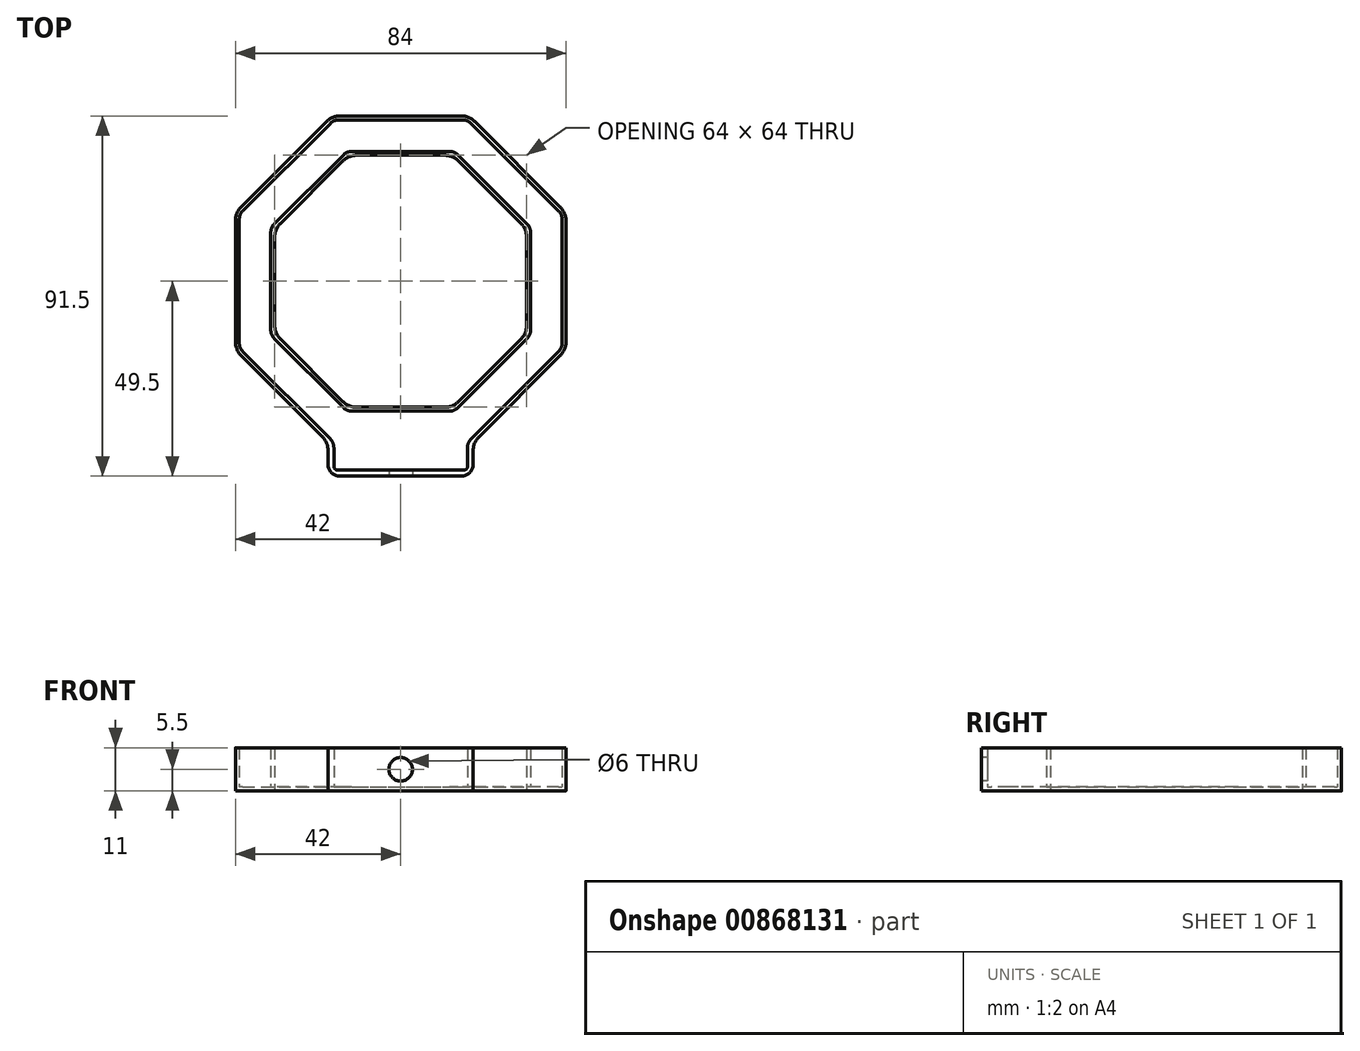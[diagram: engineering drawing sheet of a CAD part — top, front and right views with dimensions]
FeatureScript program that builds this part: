
annotation { "Feature Type Name" : "Feature", "Feature Type Description" : "" }
export const myFeature = defineFeature(function(context is Context, id is Id, definition is map)
    precondition{}
    {
        {
            var Q0;
            Q0=qCreatedBy(makeId("Top.planeOp"),FACE);
            var sketch = newSketch(context, id + "F0", { "sketchPlane" : qUnion([Q0])});
            skCircle(sketch, "E0.cCircle", {"center": v(0, 0) * mm, "radius": 41 * mm, "construction": true});
            skLineSegment(sketch, "E0.0", {"start": v(41, 16.98) * mm, "end": v(41, -16.98) * mm});
            skLineSegment(sketch, "E0.1", {"start": v(41, -16.98) * mm, "end": v(16.98, -41) * mm});
            skLineSegment(sketch, "E0.3", {"start": v(-16.98, -41) * mm, "end": v(-41, -16.98) * mm});
            skLineSegment(sketch, "E0.4", {"start": v(-41, -16.98) * mm, "end": v(-41, 16.98) * mm});
            skLineSegment(sketch, "E0.5", {"start": v(-41, 16.98) * mm, "end": v(-16.98, 41) * mm});
            skLineSegment(sketch, "E0.6", {"start": v(-16.98, 41) * mm, "end": v(16.98, 41) * mm});
            skLineSegment(sketch, "E0.7", {"start": v(16.98, 41) * mm, "end": v(41, 16.98) * mm});
            skPoint(sketch, "E0.0.midPoint", {"position": v(41, 0) * mm});
            skCircle(sketch, "E1.cCircle", {"center": v(0, 0) * mm, "radius": 33 * mm, "construction": true});
            skLineSegment(sketch, "E1.0", {"start": v(-33, 13.67) * mm, "end": v(-13.67, 33) * mm});
            skLineSegment(sketch, "E1.1", {"start": v(-13.67, 33) * mm, "end": v(13.67, 33) * mm});
            skLineSegment(sketch, "E1.2", {"start": v(13.67, 33) * mm, "end": v(33, 13.67) * mm});
            skLineSegment(sketch, "E1.3", {"start": v(33, 13.67) * mm, "end": v(33, -13.67) * mm});
            skLineSegment(sketch, "E1.4", {"start": v(33, -13.67) * mm, "end": v(13.67, -33) * mm});
            skLineSegment(sketch, "E1.5", {"start": v(13.67, -33) * mm, "end": v(-13.67, -33) * mm});
            skLineSegment(sketch, "E1.6", {"start": v(-13.67, -33) * mm, "end": v(-33, -13.67) * mm});
            skLineSegment(sketch, "E1.7", {"start": v(-33, -13.67) * mm, "end": v(-33, 13.67) * mm});
            skPoint(sketch, "E1.0.midPoint", {"position": v(-23.33, 23.33) * mm});
            skLineSegment(sketch, "E2.left", {"start": v(-16.98, -41) * mm, "end": v(-16.98, -48) * mm});
            skCircle(sketch, "E3.cCircle", {"center": v(0, 0) * mm, "radius": 32 * mm, "construction": true});
            skLineSegment(sketch, "E3.0", {"start": v(-13.25, 32) * mm, "end": v(13.25, 32) * mm});
            skLineSegment(sketch, "E3.1", {"start": v(13.25, 32) * mm, "end": v(32, 13.25) * mm});
            skLineSegment(sketch, "E3.2", {"start": v(32, 13.25) * mm, "end": v(32, -13.25) * mm});
            skLineSegment(sketch, "E3.3", {"start": v(32, -13.25) * mm, "end": v(13.25, -32) * mm});
            skLineSegment(sketch, "E3.4", {"start": v(13.25, -32) * mm, "end": v(-13.25, -32) * mm});
            skLineSegment(sketch, "E3.5", {"start": v(-13.25, -32) * mm, "end": v(-32, -13.25) * mm});
            skLineSegment(sketch, "E3.6", {"start": v(-32, -13.25) * mm, "end": v(-32, 13.25) * mm});
            skLineSegment(sketch, "E3.7", {"start": v(-32, 13.25) * mm, "end": v(-13.25, 32) * mm});
            skPoint(sketch, "E3.0.midPoint", {"position": v(0, 32) * mm});
            skCircle(sketch, "E4.cCircle", {"center": v(0, 0) * mm, "radius": 42 * mm, "construction": true});
            skLineSegment(sketch, "E4.0", {"start": v(-42, 17.4) * mm, "end": v(-17.4, 42) * mm});
            skLineSegment(sketch, "E4.1", {"start": v(-17.4, 42) * mm, "end": v(17.4, 42) * mm});
            skLineSegment(sketch, "E4.2", {"start": v(17.4, 42) * mm, "end": v(42, 17.4) * mm});
            skLineSegment(sketch, "E4.3", {"start": v(42, 17.4) * mm, "end": v(42, -17.4) * mm});
            skLineSegment(sketch, "E4.4", {"start": v(42, -17.4) * mm, "end": v(18.4, -41) * mm});
            skLineSegment(sketch, "E4.6", {"start": v(-18.48, -40.91) * mm, "end": v(-42, -17.4) * mm});
            skLineSegment(sketch, "E4.7", {"start": v(-42, -17.4) * mm, "end": v(-42, 17.4) * mm});
            skPoint(sketch, "E4.0.midPoint", {"position": v(-29.7, 29.7) * mm});
            skLineSegment(sketch, "E5", {"start": v(-18.48, -40.91) * mm, "end": v(-18.48, -49.5) * mm});
            skPoint(sketch, "E6.orphan", {"position": v(-17.4, -42) * mm});
            skLineSegment(sketch, "E7", {"start": v(-16.98, -48) * mm, "end": v(16.98, -48) * mm});
            skLineSegment(sketch, "E8", {"start": v(-18.48, -49.5) * mm, "end": v(18.4, -49.5) * mm});
            skLineSegment(sketch, "E9", {"start": v(18.4, -49.5) * mm, "end": v(18.4, -41) * mm});
            skLineSegment(sketch, "E10", {"start": v(16.98, -41) * mm, "end": v(16.98, -48) * mm});
            skSolve(sketch);
        }
        {
            var Q0;
            Q0=makeQuery(id+"F0.imprint","IMPRINT",FACE,{"disambiguationData":[TD([[makeQuery(id+"F0.imprint","IMPRINT",EDGE,{"derivedFrom":sQuery(id+"F0.wireOp",EDGE,"E0.0")}),-1.0]])]});
            extrude(context, id + "F1", {"entities" : qUnion([Q0]), "depth" : 1 * mm, "offsetDistance" : 25 * mm});
        }
        {
            var Q0;
            Q0=makeQuery(id+"F0.imprint","IMPRINT",FACE,{"disambiguationData":[TD([[makeQuery(id+"F0.imprint","IMPRINT",EDGE,{"derivedFrom":sQuery(id+"F0.wireOp",EDGE,"E1.0")}),-1.0]])]});
            var Q1;
            Q1=makeQuery(id+"F0.imprint","IMPRINT",FACE,{"disambiguationData":[TD([[makeQuery(id+"F0.imprint","IMPRINT",EDGE,{"derivedFrom":sQuery(id+"F0.wireOp",EDGE,"E0.0")}),1.0]])]});
            extrude(context, id + "F2", {"entities" : qUnion([Q0, Q1]), "operationType" : NewBodyOperationType.ADD, "depth" : 11 * mm, "offsetDistance" : 25 * mm});
        }
        {
            var Q0;
            Q0=makeQuery(id+"F2.opExtrude","SWEPT_EDGE",EDGE,{"disambiguationData":[OSD([sQuery(id+"F0.wireOp",EDGE,"E4.0"),sQuery(id+"F0.wireOp",EDGE,"E4.7")])]});
            var Q1;
            Q1=makeQuery(id+"F2.opExtrude","SWEPT_EDGE",EDGE,{"disambiguationData":[OSD([sQuery(id+"F0.wireOp",EDGE,"E4.6"),sQuery(id+"F0.wireOp",EDGE,"E4.7")])]});
            var Q2;
            Q2=makeQuery(id+"F2.opExtrude","SWEPT_EDGE",EDGE,{"disambiguationData":[OSD([sQuery(id+"F0.wireOp",EDGE,"E4.0"),sQuery(id+"F0.wireOp",EDGE,"E4.1")])]});
            var Q3;
            Q3=makeQuery(id+"F2.opExtrude","SWEPT_EDGE",EDGE,{"disambiguationData":[OSD([sQuery(id+"F0.wireOp",EDGE,"E4.1"),sQuery(id+"F0.wireOp",EDGE,"E4.2")])]});
            var Q4;
            Q4=makeQuery(id+"F2.opExtrude","SWEPT_EDGE",EDGE,{"disambiguationData":[OSD([sQuery(id+"F0.wireOp",EDGE,"E4.2"),sQuery(id+"F0.wireOp",EDGE,"E4.3")])]});
            var Q5;
            Q5=makeQuery(id+"F2.opExtrude","SWEPT_EDGE",EDGE,{"disambiguationData":[OSD([sQuery(id+"F0.wireOp",EDGE,"E4.3"),sQuery(id+"F0.wireOp",EDGE,"E4.4")])]});
            var Q6;
            Q6=makeQuery(id+"F2.opExtrude","SWEPT_EDGE",EDGE,{"disambiguationData":[OSD([sQuery(id+"F0.wireOp",EDGE,"E3.0"),sQuery(id+"F0.wireOp",EDGE,"E3.7")])]});
            var Q7;
            Q7=makeQuery(id+"F2.opExtrude","SWEPT_EDGE",EDGE,{"disambiguationData":[OSD([sQuery(id+"F0.wireOp",EDGE,"E3.6"),sQuery(id+"F0.wireOp",EDGE,"E3.7")])]});
            var Q8;
            Q8=makeQuery(id+"F2.opExtrude","SWEPT_EDGE",EDGE,{"disambiguationData":[OSD([sQuery(id+"F0.wireOp",EDGE,"E3.5"),sQuery(id+"F0.wireOp",EDGE,"E3.6")])]});
            var Q9;
            Q9=makeQuery(id+"F2.opExtrude","SWEPT_EDGE",EDGE,{"disambiguationData":[OSD([sQuery(id+"F0.wireOp",EDGE,"E3.4"),sQuery(id+"F0.wireOp",EDGE,"E3.5")])]});
            var Q10;
            Q10=makeQuery(id+"F2.opExtrude","SWEPT_EDGE",EDGE,{"disambiguationData":[OSD([sQuery(id+"F0.wireOp",EDGE,"E3.3"),sQuery(id+"F0.wireOp",EDGE,"E3.4")])]});
            var Q11;
            Q11=makeQuery(id+"F2.opExtrude","SWEPT_EDGE",EDGE,{"disambiguationData":[OSD([sQuery(id+"F0.wireOp",EDGE,"E3.2"),sQuery(id+"F0.wireOp",EDGE,"E3.3")])]});
            var Q12;
            Q12=makeQuery(id+"F2.opExtrude","SWEPT_EDGE",EDGE,{"disambiguationData":[OSD([sQuery(id+"F0.wireOp",EDGE,"E3.1"),sQuery(id+"F0.wireOp",EDGE,"E3.2")])]});
            var Q13;
            Q13=makeQuery(id+"F2.opExtrude","SWEPT_EDGE",EDGE,{"disambiguationData":[OSD([sQuery(id+"F0.wireOp",EDGE,"E3.0"),sQuery(id+"F0.wireOp",EDGE,"E3.1")])]});
            var Q14;
            Q14=makeQuery(id+"F2.opExtrude","SWEPT_EDGE",EDGE,{"disambiguationData":[OSD([sQuery(id+"F0.wireOp",EDGE,"E4.4"),sQuery(id+"F0.wireOp",EDGE,"E9")])]});
            var Q15;
            Q15=makeQuery(id+"F2.opExtrude","SWEPT_EDGE",EDGE,{"disambiguationData":[OSD([sQuery(id+"F0.wireOp",EDGE,"E4.6"),sQuery(id+"F0.wireOp",EDGE,"E5")])]});
            fillet(context, id + "F3", {"entities" : qUnion([Q0, Q1, Q2, Q3, Q4, Q5, Q6, Q7, Q8, Q9, Q10, Q11, Q12, Q13, Q14, Q15]), "radius" : 5 * mm, "tangentPropagation" : true, "allowEdgeOverflow" : false});
        }
        {
            var Q0;
            Q0=makeQuery(id+"F2.opExtrude","SWEPT_EDGE",EDGE,{"disambiguationData":[OSD([sQuery(id+"F0.wireOp",EDGE,"E1.6"),sQuery(id+"F0.wireOp",EDGE,"E1.7")])]});
            var Q1;
            Q1=makeQuery(id+"F2.opExtrude","SWEPT_EDGE",EDGE,{"disambiguationData":[OSD([sQuery(id+"F0.wireOp",EDGE,"E1.5"),sQuery(id+"F0.wireOp",EDGE,"E1.6")])]});
            var Q2;
            Q2=makeQuery(id+"F2.opExtrude","SWEPT_EDGE",EDGE,{"disambiguationData":[OSD([sQuery(id+"F0.wireOp",EDGE,"E1.4"),sQuery(id+"F0.wireOp",EDGE,"E1.5")])]});
            var Q3;
            Q3=makeQuery(id+"F2.opExtrude","SWEPT_EDGE",EDGE,{"disambiguationData":[OSD([sQuery(id+"F0.wireOp",EDGE,"E1.3"),sQuery(id+"F0.wireOp",EDGE,"E1.4")])]});
            var Q4;
            Q4=makeQuery(id+"F2.opExtrude","SWEPT_EDGE",EDGE,{"disambiguationData":[OSD([sQuery(id+"F0.wireOp",EDGE,"E1.2"),sQuery(id+"F0.wireOp",EDGE,"E1.3")])]});
            var Q5;
            Q5=makeQuery(id+"F2.opExtrude","SWEPT_EDGE",EDGE,{"disambiguationData":[OSD([sQuery(id+"F0.wireOp",EDGE,"E1.1"),sQuery(id+"F0.wireOp",EDGE,"E1.2")])]});
            var Q6;
            Q6=makeQuery(id+"F2.opExtrude","SWEPT_EDGE",EDGE,{"disambiguationData":[OSD([sQuery(id+"F0.wireOp",EDGE,"E1.0"),sQuery(id+"F0.wireOp",EDGE,"E1.1")])]});
            var Q7;
            Q7=makeQuery(id+"F2.opExtrude","SWEPT_EDGE",EDGE,{"disambiguationData":[OSD([sQuery(id+"F0.wireOp",EDGE,"E1.0"),sQuery(id+"F0.wireOp",EDGE,"E1.7")])]});
            var Q8;
            Q8=makeQuery(id+"F2.opExtrude","SWEPT_EDGE",EDGE,{"disambiguationData":[OSD([sQuery(id+"F0.wireOp",EDGE,"E0.0"),sQuery(id+"F0.wireOp",EDGE,"E0.1")])]});
            var Q9;
            Q9=makeQuery(id+"F2.opExtrude","SWEPT_EDGE",EDGE,{"disambiguationData":[OSD([sQuery(id+"F0.wireOp",EDGE,"E0.0"),sQuery(id+"F0.wireOp",EDGE,"E0.7")])]});
            var Q10;
            Q10=makeQuery(id+"F2.opExtrude","SWEPT_EDGE",EDGE,{"disambiguationData":[OSD([sQuery(id+"F0.wireOp",EDGE,"E0.6"),sQuery(id+"F0.wireOp",EDGE,"E0.7")])]});
            var Q11;
            Q11=makeQuery(id+"F2.opExtrude","SWEPT_EDGE",EDGE,{"disambiguationData":[OSD([sQuery(id+"F0.wireOp",EDGE,"E0.5"),sQuery(id+"F0.wireOp",EDGE,"E0.6")])]});
            var Q12;
            Q12=makeQuery(id+"F2.opExtrude","SWEPT_EDGE",EDGE,{"disambiguationData":[OSD([sQuery(id+"F0.wireOp",EDGE,"E0.4"),sQuery(id+"F0.wireOp",EDGE,"E0.5")])]});
            var Q13;
            Q13=makeQuery(id+"F2.opExtrude","SWEPT_EDGE",EDGE,{"disambiguationData":[OSD([sQuery(id+"F0.wireOp",EDGE,"E0.3"),sQuery(id+"F0.wireOp",EDGE,"E0.4")])]});
            var Q14;
            Q14=makeQuery(id+"F2.opExtrude","SWEPT_EDGE",EDGE,{"disambiguationData":[OSD([sQuery(id+"F0.wireOp",EDGE,"E0.3"),sQuery(id+"F0.wireOp",EDGE,"E2.left")])]});
            var Q15;
            Q15=makeQuery(id+"F2.opExtrude","SWEPT_EDGE",EDGE,{"disambiguationData":[OSD([sQuery(id+"F0.wireOp",EDGE,"E0.1"),sQuery(id+"F0.wireOp",EDGE,"E10")])]});
            var Q16;
            Q16=makeQuery(id+"F2.opExtrude","SWEPT_EDGE",EDGE,{"disambiguationData":[OSD([sQuery(id+"F0.wireOp",EDGE,"E8"),sQuery(id+"F0.wireOp",EDGE,"E9")])]});
            var Q17;
            Q17=makeQuery(id+"F2.opExtrude","SWEPT_EDGE",EDGE,{"disambiguationData":[OSD([sQuery(id+"F0.wireOp",EDGE,"E5"),sQuery(id+"F0.wireOp",EDGE,"E8")])]});
            fillet(context, id + "F4", {"entities" : qUnion([Q0, Q1, Q2, Q3, Q4, Q5, Q6, Q7, Q8, Q9, Q10, Q11, Q12, Q13, Q14, Q15, Q16, Q17]), "radius" : 3 * mm, "tangentPropagation" : true, "allowEdgeOverflow" : false});
        }
        {
            var Q0;
            Q0=makeQuery(id+"F2.opExtrude","SWEPT_FACE",FACE,{"disambiguationData":[OSD([sQuery(id+"F0.wireOp",EDGE,"E8")])]});
            var sketch = newSketch(context, id + "F5", { "sketchPlane" : qUnion([Q0])});
            skCircle(sketch, "E11", {"center": v(0, 5.5) * mm, "radius": 3 * mm});
            skPoint(sketch, "E11.centerSnap0", {"position": v(-15.48, 5.5) * mm});
            skSolve(sketch);
        }
        {
            var Q0;
            Q0=makeQuery(id+"F5.imprint","IMPRINT",FACE,{"disambiguationData":[TD([[makeQuery(id+"F5.imprint","IMPRINT",EDGE,{"derivedFrom":sQuery(id+"F5.wireOp",EDGE,"E11")}),1.0]])]});
            extrude(context, id + "F6", {"entities" : qUnion([Q0]), "operationType" : NewBodyOperationType.REMOVE, "oppositeDirection" : true, "depth" : 2 * mm, "offsetDistance" : 25 * mm});
        }
        {
            var Q0;
            Q0=makeQuery(id+"F2.opExtrude","SWEPT_EDGE",EDGE,{"disambiguationData":[OSD([sQuery(id+"F0.wireOp",EDGE,"E2.left"),sQuery(id+"F0.wireOp",EDGE,"E7")])]});
            var Q1;
            Q1=makeQuery(id+"F2.opExtrude","SWEPT_EDGE",EDGE,{"disambiguationData":[OSD([sQuery(id+"F0.wireOp",EDGE,"E7"),sQuery(id+"F0.wireOp",EDGE,"E10")])]});
            fillet(context, id + "F7", {"entities" : qUnion([Q0, Q1]), "radius" : 1 * mm, "tangentPropagation" : true, "allowEdgeOverflow" : false});
        }
    });
